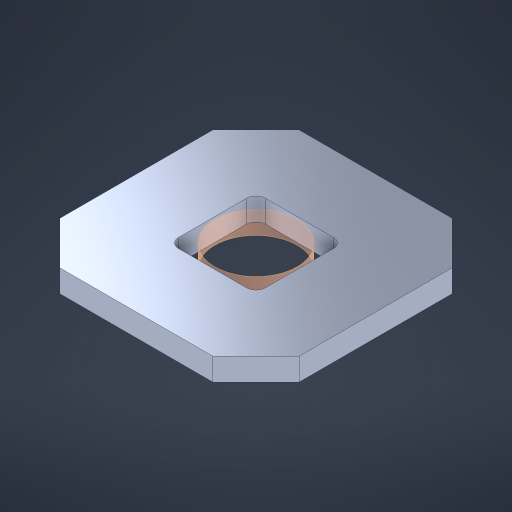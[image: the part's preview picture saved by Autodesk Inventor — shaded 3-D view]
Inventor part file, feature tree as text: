
AUTODESK INVENTOR PART (.ipt)
format: ipt  version: 2023 (Build 270158000, 158)  size: 270,336 bytes
history: native  units: in
note: dims shown in document units (in); Inventor stores cm internally (conversion verified against a paired STEP export)
features: sketch x2, other x2, pattern_linear x1
ambient origin geometry x8: Origin, YZ Plane, XZ Plane, XY Plane, X Axis, Y Axis, Z Axis, Center Point
bodies: Solid1 (feature_tree), Body (feature_tree)
feature tree (5):
  pattern_linear  "Rectangular Pattern1"  Spacing1=0.09in  [1 undecoded]
  sketch  "Sketch1"  dims[d1=0.5in]
  sketch  "Sketch2"  dims[d2=0.182in d3=0.09in d4=0.09in d5=0.09in d6=0.09in d7=0.09in d8=0.09in d9=0.09in d10=0.09in d11=0.02in d13=0.0in d14=0.172in d15=0.0625in d16=0.0in d19=0.5in d22=0.5in]
  other  "Srf1"
  other  "Circle"
note: 1 required parameter value undecoded (feature->parameter linkage not recoverable at this tier; creation-order binding heuristic only, values carry confidence <= 0.55)
